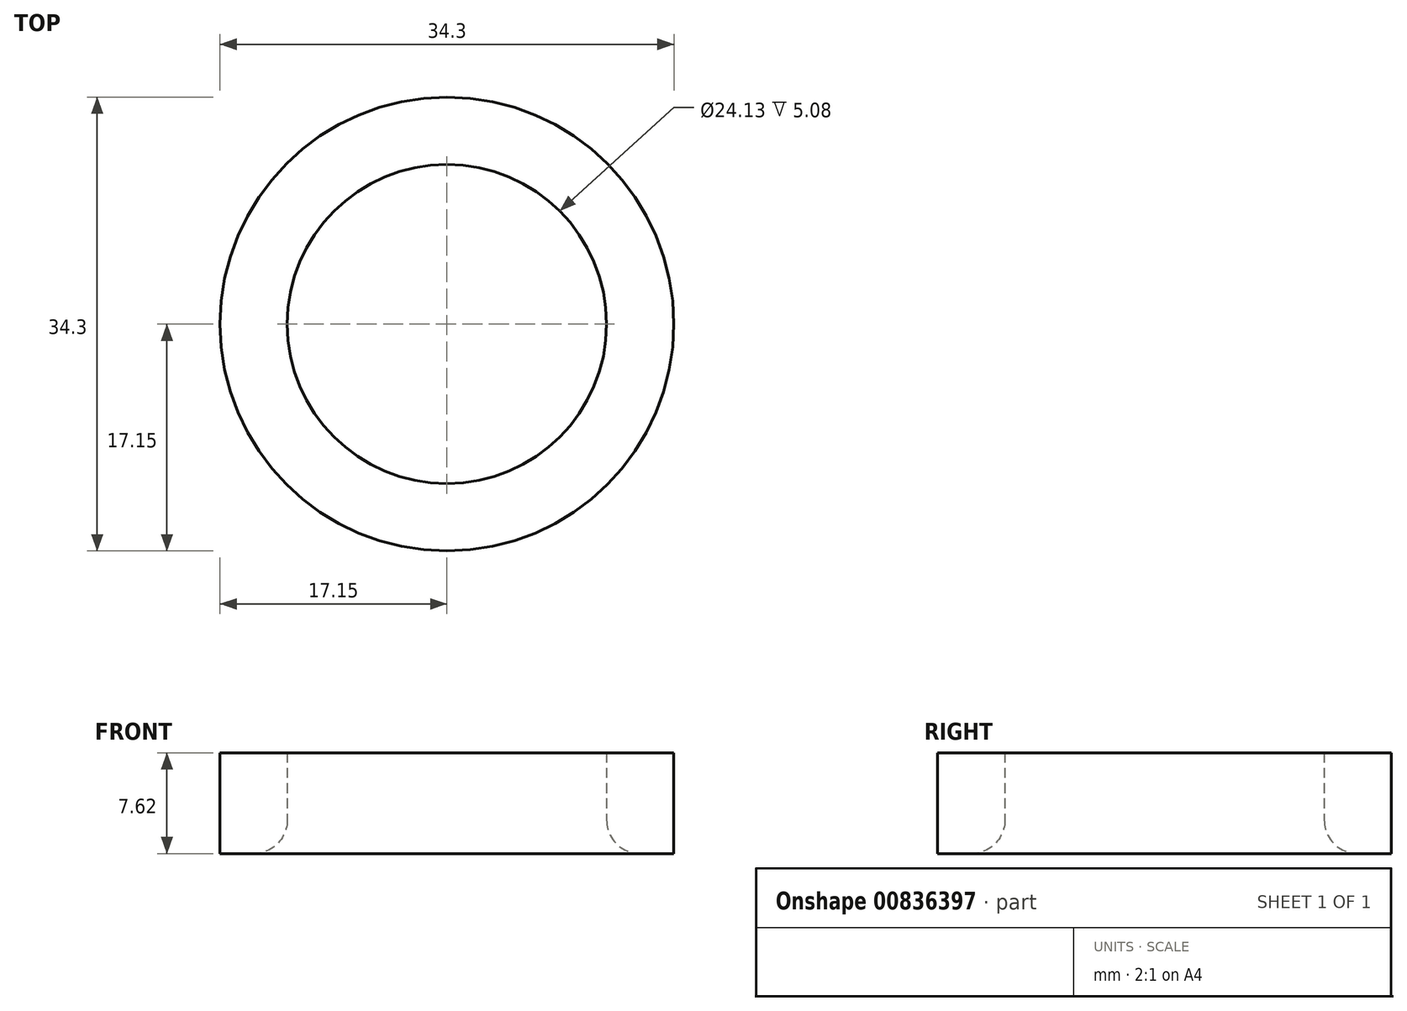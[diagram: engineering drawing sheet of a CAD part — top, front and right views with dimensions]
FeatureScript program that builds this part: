
annotation { "Feature Type Name" : "Feature", "Feature Type Description" : "" }
export const myFeature = defineFeature(function(context is Context, id is Id, definition is map)
    precondition{}
    {
        {
            var Q0;
            Q0=qCreatedBy(makeId("Top.planeOp"),FACE);
            var sketch = newSketch(context, id + "F0", { "sketchPlane" : qUnion([Q0])});
            skCircle(sketch, "E0", {"center": v(0, 0) * mm, "radius": 12.07 * mm});
            skCircle(sketch, "E1", {"center": v(0, 0) * mm, "radius": 17.15 * mm});
            skSolve(sketch);
        }
        {
            var Q0;
            Q0=makeQuery(id+"F0.imprint","IMPRINT",FACE,{"disambiguationData":[TD([[makeQuery(id+"F0.imprint","IMPRINT",EDGE,{"derivedFrom":sQuery(id+"F0.wireOp",EDGE,"E0")}),-1.0]])]});
            extrude(context, id + "F1", {"entities" : qUnion([Q0]), "depth" : 7.62 * mm, "offsetDistance" : 25.4 * mm});
        }
        {
            var Q0;
            Q0=makeQuery(id+"F1.opExtrude","CAP_EDGE",EDGE,{"disambiguationData":[OSD([sQuery(id+"F0.wireOp",EDGE,"E0")])],"isStart":true});
            fillet(context, id + "F2", {"entities" : qUnion([Q0]), "radius" : 2.54 * mm, "tangentPropagation" : true, "allowEdgeOverflow" : false});
        }
    });
